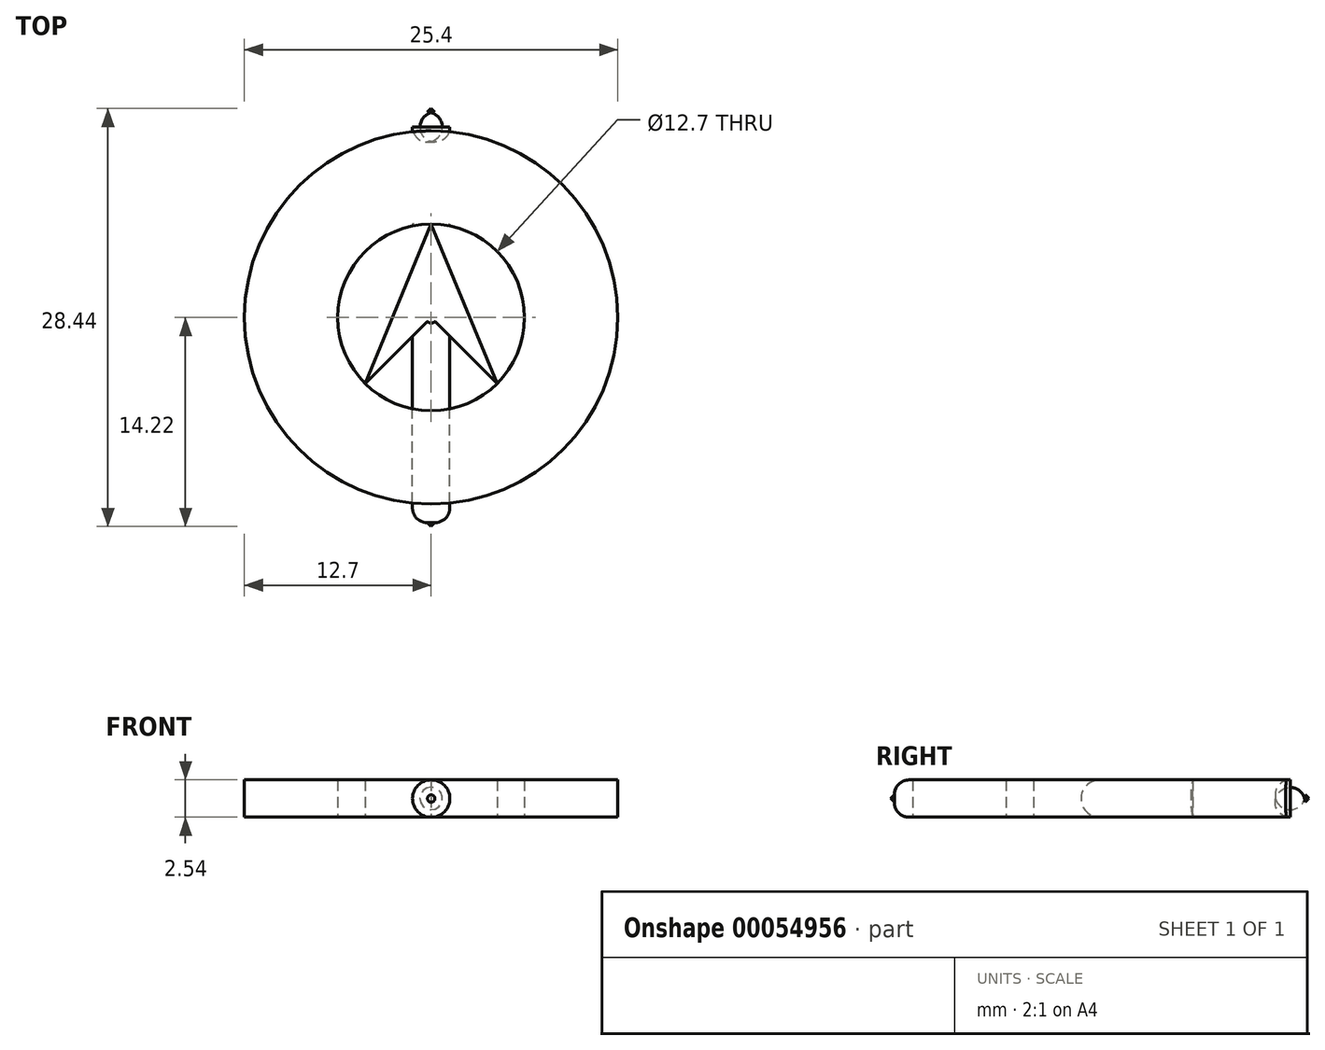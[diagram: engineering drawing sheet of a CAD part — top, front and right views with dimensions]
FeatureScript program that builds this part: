
annotation { "Feature Type Name" : "Feature", "Feature Type Description" : "" }
export const myFeature = defineFeature(function(context is Context, id is Id, definition is map)
    precondition{}
    {
        {
            var Q0;
            Q0=qCreatedBy(makeId("Top.planeOp"),FACE);
            var sketch = newSketch(context, id + "F0", { "sketchPlane" : qUnion([Q0])});
            skCircle(sketch, "E0", {"center": v(0, 0) * mm, "radius": 12.7 * mm});
            skCircle(sketch, "E1", {"center": v(0, 0) * mm, "radius": 6.35 * mm});
            skSolve(sketch);
        }
        {
            var Q0;
            Q0 = qSketchRegion(id + "F0", true);
            extrude(context, id + "F1", {"entities" : qUnion([Q0]), "depth" : 2.54 * mm});
        }
        {
            var Q0;
            Q0=qCreatedBy(makeId("Front.planeOp"),FACE);
            var sketch = newSketch(context, id + "F2", { "sketchPlane" : qUnion([Q0])});
            skCircle(sketch, "E2", {"center": v(0, 1.27) * mm, "radius": 1.27 * mm});
            skSolve(sketch);
        }
        {
            var Q0;
            Q0 = qSketchRegion(id + "F2", true);
            extrude(context, id + "F3", {"entities" : qUnion([Q0]), "operationType" : NewBodyOperationType.ADD, "oppositeDirection" : true, "depth" : 13.97 * mm});
        }
        {
            var Q0;
            Q0=makeQuery(id+"F3.opExtrude","CAP_EDGE",EDGE,{"disambiguationData":[OSD([sQuery(id+"F2.wireOp",EDGE,"E2")])],"isStart":false});
            fillet(context, id + "F4", {"entities" : qUnion([Q0]), "radius" : 1.02 * mm, "tangentPropagation" : true, "allowEdgeOverflow" : false});
        }
        {
            var Q0;
            Q0=makeQuery(id+"F3.opExtrude","CAP_FACE",FACE,{"disambiguationData":[OSD([sQuery(id+"F2.wireOp",EDGE,"E2")])],"isStart":true});
            var sketch = newSketch(context, id + "F5", { "sketchPlane" : qUnion([Q0])});
            skSolve(sketch);
        }
        {
            var Q0;
            Q0=makeQuery(id+"F5.imprint","IMPRINT",FACE,{"disambiguationData":[TD([[makeQuery(id+"F5.imprint","IMPRINT",EDGE,{"derivedFrom":makeQuery(id+"F3.opExtrude","CAP_EDGE",EDGE,{"disambiguationData":[OSD([sQuery(id+"F2.wireOp",EDGE,"E2")])],"isStart":true})}),1.0]])]});
            var sketch = newSketch(context, id + "F6", { "sketchPlane" : qUnion([Q0])});
            skCircle(sketch, "E3", {"center": v(0, 1.27) * mm, "radius": 1.27 * mm});
            skSolve(sketch);
        }
        {
            var Q0;
            Q0 = qSketchRegion(id + "F6", true);
            extrude(context, id + "F7", {"entities" : qUnion([Q0]), "operationType" : NewBodyOperationType.REMOVE, "oppositeDirection" : true, "depth" : 6.35 * mm});
        }
        {
            var Q0;
            Q0=makeQuery(id+"F1.opExtrude","CAP_FACE",FACE,{"disambiguationData":[OSD([sQuery(id+"F0.wireOp",EDGE,"E0"),sQuery(id+"F0.wireOp",EDGE,"E1")])],"isStart":true});
            var sketch = newSketch(context, id + "F8", { "sketchPlane" : qUnion([Q0])});
            skLineSegment(sketch, "E4", {"start": v(0, 0) * mm, "end": v(-4.5, 4.5) * mm});
            skLineSegment(sketch, "E5", {"start": v(0, 0) * mm, "end": v(4.5, 4.5) * mm});
            skLineSegment(sketch, "E6", {"start": v(0, -6.35) * mm, "end": v(4.5, 4.5) * mm});
            skLineSegment(sketch, "E7", {"start": v(-4.5, 4.5) * mm, "end": v(0, -6.35) * mm});
            skSolve(sketch);
        }
        {
            var Q0;
            Q0 = qSketchRegion(id + "F8", true);
            extrude(context, id + "F9", {"entities" : qUnion([Q0]), "oppositeDirection" : true, "depth" : 2.54 * mm});
        }
        {
            var Q0;
            Q0=makeQuery(id+"F3.opExtrude","CAP_FACE",FACE,{"disambiguationData":[OSD([sQuery(id+"F2.wireOp",EDGE,"E2")])],"isStart":false});
            var sketch = newSketch(context, id + "F10", { "sketchPlane" : qUnion([Q0])});
            skCircle(sketch, "E8", {"center": v(0, 1.27) * mm, "radius": 0.25 * mm});
            skSolve(sketch);
        }
        {
            var Q0;
            Q0 = qSketchRegion(id + "F10", true);
            extrude(context, id + "F11", {"entities" : qUnion([Q0]), "operationType" : NewBodyOperationType.ADD, "depth" : 0.25 * mm});
        }
        {
            var Q0;
            Q0=makeQuery(id+"F11.opExtrude","CAP_EDGE",EDGE,{"disambiguationData":[OSD([sQuery(id+"F10.wireOp",EDGE,"E8")])],"isStart":false});
            chamfer(context, id + "F12", {"entities" : qUnion([Q0]), "width" : 0.25 * mm, "tangentPropagation" : true});
        }
        {
            var Q0;
            Q0=qCreatedBy(makeId("Front.planeOp"),FACE);
            var sketch = newSketch(context, id + "F13", { "sketchPlane" : qUnion([Q0])});
            skCircle(sketch, "E9", {"center": v(0, 1.27) * mm, "radius": 1.27 * mm});
            skSolve(sketch);
        }
        {
            var Q0;
            Q0 = qSketchRegion(id + "F13", true);
            extrude(context, id + "F14", {"entities" : qUnion([Q0]), "depth" : 13.97 * mm});
        }
        {
            var Q0;
            Q0=makeQuery(id+"F14.opExtrude","CAP_EDGE",EDGE,{"disambiguationData":[OSD([sQuery(id+"F13.wireOp",EDGE,"E9")])],"isStart":false});
            fillet(context, id + "F15", {"entities" : qUnion([Q0]), "radius" : 1.02 * mm, "tangentPropagation" : true, "allowEdgeOverflow" : false});
        }
        {
            var Q0;
            Q0=makeQuery(id+"F14.opExtrude","CAP_FACE",FACE,{"disambiguationData":[OSD([sQuery(id+"F13.wireOp",EDGE,"E9")])],"isStart":false});
            var sketch = newSketch(context, id + "F16", { "sketchPlane" : qUnion([Q0])});
            skCircle(sketch, "E10", {"center": v(0, 1.27) * mm, "radius": 0.25 * mm});
            skSolve(sketch);
        }
        {
            var Q0;
            Q0 = qSketchRegion(id + "F16", true);
            extrude(context, id + "F17", {"entities" : qUnion([Q0]), "operationType" : NewBodyOperationType.ADD, "depth" : 0.25 * mm});
        }
        {
            var Q0;
            Q0=makeQuery(id+"F17.opExtrude","CAP_EDGE",EDGE,{"disambiguationData":[OSD([sQuery(id+"F16.wireOp",EDGE,"E10")])],"isStart":false});
            chamfer(context, id + "F18", {"entities" : qUnion([Q0]), "width" : 0.25 * mm, "tangentPropagation" : true});
        }
        {
            var Q0;
            Q0=makeQuery(id+"F9.opExtrude","CAP_FACE",FACE,{"disambiguationData":[OSD([sQuery(id+"F8.wireOp",EDGE,"E4"),sQuery(id+"F8.wireOp",EDGE,"E5"),sQuery(id+"F8.wireOp",EDGE,"E6"),sQuery(id+"F8.wireOp",EDGE,"E7")])],"isStart":false});
            var sketch = newSketch(context, id + "F19", { "sketchPlane" : qUnion([Q0])});
            skCircle(sketch, "E11", {"center": v(0, 0) * mm, "radius": 0.38 * mm});
            skSolve(sketch);
        }
        {
            var Q0;
            Q0 = qSketchRegion(id + "F19", true);
            extrude(context, id + "F20", {"entities" : qUnion([Q0]), "operationType" : NewBodyOperationType.ADD, "oppositeDirection" : true, "depth" : 2.54 * mm});
        }
    });
